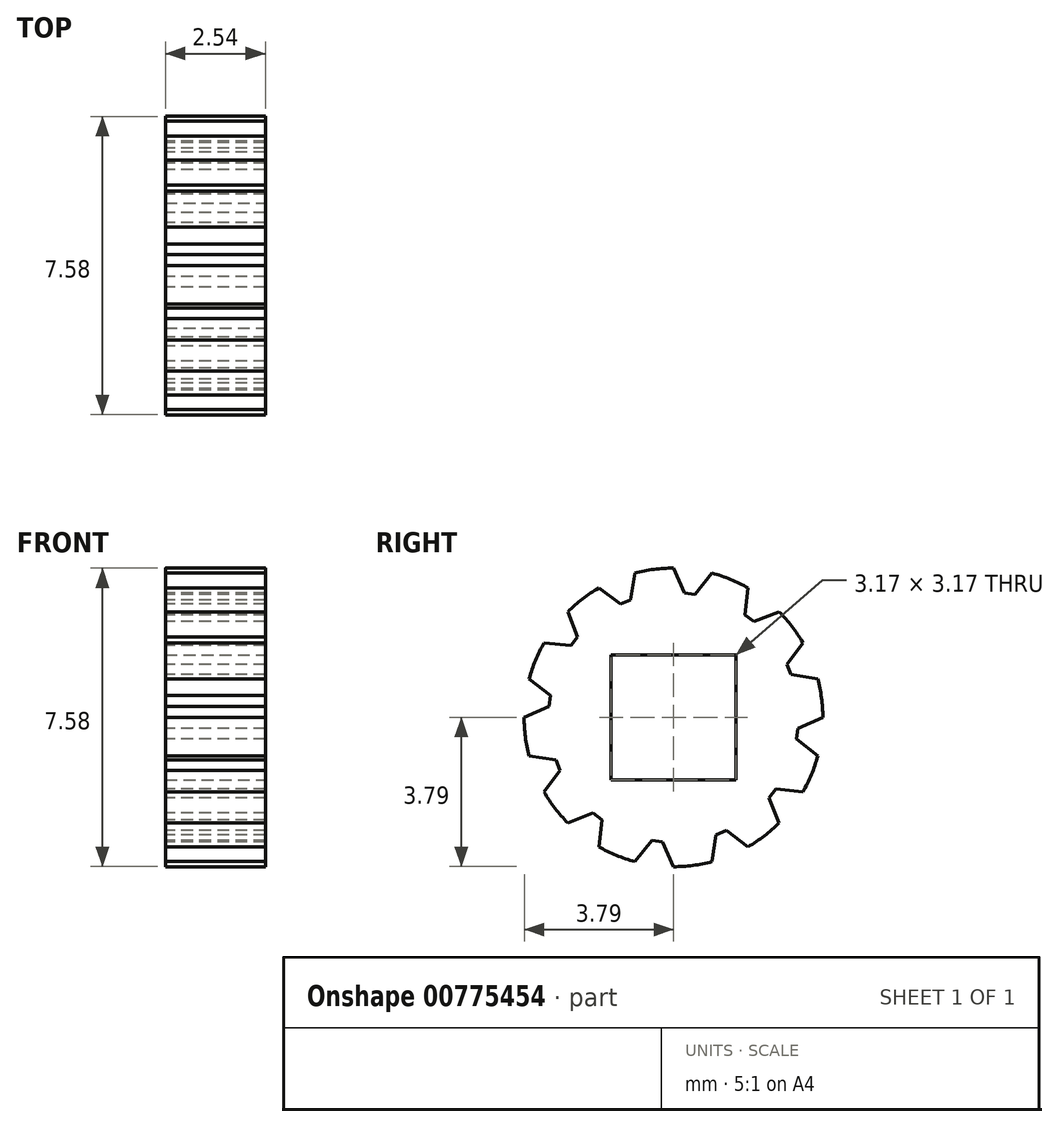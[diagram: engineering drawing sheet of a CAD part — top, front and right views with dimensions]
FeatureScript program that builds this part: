
annotation { "Feature Type Name" : "Feature", "Feature Type Description" : "" }
export const myFeature = defineFeature(function(context is Context, id is Id, definition is map)
    precondition{}
    {
        {
            var Q0;
            Q0=qCreatedBy(makeId("Right.planeOp"),FACE);
            var sketch = newSketch(context, id + "F0", { "sketchPlane" : qUnion([Q0])});
            skLineSegment(sketch, "E0", {"start": v(0, 0) * mm, "end": v(-3.8, 0) * mm});
            skLineSegment(sketch, "E1", {"start": v(0, 0) * mm, "end": v(-3.66, 0.98) * mm});
            skLineSegment(sketch, "E2", {"start": v(0, 0) * mm, "end": v(-3.16, 0.28) * mm});
            skLineSegment(sketch, "E3", {"start": v(0, 0) * mm, "end": v(-3.13, 0.55) * mm});
            skLineSegment(sketch, "E4", {"start": v(-3.16, 0.28) * mm, "end": v(-3.13, 0.55) * mm});
            skLineSegment(sketch, "E5", {"start": v(-3.13, 0.55) * mm, "end": v(-3.66, 0.98) * mm});
            skLineSegment(sketch, "E6", {"start": v(-3.16, 0.28) * mm, "end": v(-3.8, 0) * mm});
            skArc(sketch, "E7", {"start": v(-3.66, 0.98) * mm, "mid": v(-3.76, 0.5) * mm, "end": v(-3.8, 0) * mm});
            skArc(sketch, "E8", {"start": v(-3.8, 0) * mm, "mid": v(3.76, -0.5) * mm, "end": v(-3.66, 0.98) * mm});
            skArc(sketch, "E9.1.3", {"start": v(0.98, -3.66) * mm, "mid": v(1.45, -3.5) * mm, "end": v(1.9, -3.29) * mm});
            skArc(sketch, "E10.2.3", {"start": v(2.68, 2.68) * mm, "mid": v(2.3, 3) * mm, "end": v(1.9, 3.29) * mm});
            skArc(sketch, "E11.1.0", {"start": v(-3.66, -0.98) * mm, "mid": v(-3.5, -1.45) * mm, "end": v(-3.29, -1.9) * mm});
            skLineSegment(sketch, "E11.1.1", {"start": v(-2.98, -1.09) * mm, "end": v(-3.66, -0.98) * mm});
            skLineSegment(sketch, "E11.1.2", {"start": v(-2.88, -1.34) * mm, "end": v(-2.98, -1.09) * mm});
            skLineSegment(sketch, "E11.1.3", {"start": v(-2.88, -1.34) * mm, "end": v(-3.29, -1.9) * mm});
            skArc(sketch, "E11.2.0", {"start": v(-2.68, -2.68) * mm, "mid": v(-2.3, -3) * mm, "end": v(-1.9, -3.29) * mm});
            skLineSegment(sketch, "E11.2.1", {"start": v(-2.04, -2.43) * mm, "end": v(-2.68, -2.68) * mm});
            skLineSegment(sketch, "E11.2.2", {"start": v(-1.82, -2.6) * mm, "end": v(-2.04, -2.43) * mm});
            skLineSegment(sketch, "E11.2.3", {"start": v(-1.82, -2.6) * mm, "end": v(-1.9, -3.29) * mm});
            skArc(sketch, "E11.3.0", {"start": v(-0.98, -3.66) * mm, "mid": v(-0.5, -3.76) * mm, "end": v(0, -3.8) * mm});
            skLineSegment(sketch, "E11.3.1", {"start": v(-0.55, -3.13) * mm, "end": v(-0.98, -3.66) * mm});
            skLineSegment(sketch, "E11.3.2", {"start": v(-0.28, -3.16) * mm, "end": v(-0.55, -3.13) * mm});
            skLineSegment(sketch, "E11.3.3", {"start": v(-0.28, -3.16) * mm, "end": v(0, -3.8) * mm});
            skLineSegment(sketch, "E11.4.1", {"start": v(1.09, -2.98) * mm, "end": v(0.98, -3.66) * mm});
            skLineSegment(sketch, "E11.4.2", {"start": v(1.34, -2.88) * mm, "end": v(1.09, -2.98) * mm});
            skLineSegment(sketch, "E11.4.3", {"start": v(1.34, -2.88) * mm, "end": v(1.9, -3.29) * mm});
            skArc(sketch, "E11.5.0", {"start": v(2.68, -2.68) * mm, "mid": v(3, -2.3) * mm, "end": v(3.29, -1.9) * mm});
            skLineSegment(sketch, "E11.5.1", {"start": v(2.43, -2.04) * mm, "end": v(2.68, -2.68) * mm});
            skLineSegment(sketch, "E11.5.2", {"start": v(2.6, -1.82) * mm, "end": v(2.43, -2.04) * mm});
            skLineSegment(sketch, "E11.5.3", {"start": v(2.6, -1.82) * mm, "end": v(3.29, -1.9) * mm});
            skArc(sketch, "E11.6.0", {"start": v(3.66, -0.98) * mm, "mid": v(3.76, -0.5) * mm, "end": v(3.8, 0) * mm});
            skLineSegment(sketch, "E11.6.1", {"start": v(3.13, -0.55) * mm, "end": v(3.66, -0.98) * mm});
            skLineSegment(sketch, "E11.6.2", {"start": v(3.16, -0.28) * mm, "end": v(3.13, -0.55) * mm});
            skLineSegment(sketch, "E11.6.3", {"start": v(3.16, -0.28) * mm, "end": v(3.8, 0) * mm});
            skArc(sketch, "E11.7.0", {"start": v(3.66, 0.98) * mm, "mid": v(3.5, 1.45) * mm, "end": v(3.29, 1.9) * mm});
            skLineSegment(sketch, "E11.7.1", {"start": v(2.98, 1.09) * mm, "end": v(3.66, 0.98) * mm});
            skLineSegment(sketch, "E11.7.2", {"start": v(2.88, 1.34) * mm, "end": v(2.98, 1.09) * mm});
            skLineSegment(sketch, "E11.7.3", {"start": v(2.88, 1.34) * mm, "end": v(3.29, 1.9) * mm});
            skLineSegment(sketch, "E11.8.1", {"start": v(2.04, 2.43) * mm, "end": v(2.68, 2.68) * mm});
            skLineSegment(sketch, "E11.8.2", {"start": v(1.82, 2.6) * mm, "end": v(2.04, 2.43) * mm});
            skLineSegment(sketch, "E11.8.3", {"start": v(1.82, 2.6) * mm, "end": v(1.9, 3.29) * mm});
            skArc(sketch, "E11.9.0", {"start": v(0.98, 3.66) * mm, "mid": v(0.5, 3.76) * mm, "end": v(0, 3.8) * mm});
            skLineSegment(sketch, "E11.9.1", {"start": v(0.55, 3.13) * mm, "end": v(0.98, 3.66) * mm});
            skLineSegment(sketch, "E11.9.2", {"start": v(0.28, 3.16) * mm, "end": v(0.55, 3.13) * mm});
            skLineSegment(sketch, "E11.9.3", {"start": v(0.28, 3.16) * mm, "end": v(0, 3.8) * mm});
            skArc(sketch, "E11.10.0", {"start": v(-0.98, 3.66) * mm, "mid": v(-1.45, 3.5) * mm, "end": v(-1.9, 3.29) * mm});
            skLineSegment(sketch, "E11.10.1", {"start": v(-1.09, 2.98) * mm, "end": v(-0.98, 3.66) * mm});
            skLineSegment(sketch, "E11.10.2", {"start": v(-1.34, 2.88) * mm, "end": v(-1.09, 2.98) * mm});
            skLineSegment(sketch, "E11.10.3", {"start": v(-1.34, 2.88) * mm, "end": v(-1.9, 3.29) * mm});
            skArc(sketch, "E11.11.0", {"start": v(-2.68, 2.68) * mm, "mid": v(-3, 2.3) * mm, "end": v(-3.29, 1.9) * mm});
            skLineSegment(sketch, "E11.11.1", {"start": v(-2.43, 2.04) * mm, "end": v(-2.68, 2.68) * mm});
            skLineSegment(sketch, "E11.11.2", {"start": v(-2.6, 1.82) * mm, "end": v(-2.43, 2.04) * mm});
            skLineSegment(sketch, "E11.11.3", {"start": v(-2.6, 1.82) * mm, "end": v(-3.29, 1.9) * mm});
            skSolve(sketch);
        }
        {
            var Q0;
            {var subQ24=sQuery(id+"F0.wireOp",EDGE,"E0");Q0=makeQuery(id+"F0.imprint","IMPRINT",FACE,{"disambiguationData":[TD([[makeQuery(id+"F0.imprint","IMPRINT",EDGE,{"derivedFrom":subQ24}),1.0]])]});}
            var Q1;
            Q1=makeQuery(id+"F0.imprint","IMPRINT",FACE,{"disambiguationData":[TD([[makeQuery(id+"F0.imprint","IMPRINT",EDGE,{"derivedFrom":sQuery(id+"F0.wireOp",EDGE,"E0")}),-1.0]])]});
            var Q2;
            Q2=makeQuery(id+"F0.imprint","IMPRINT",FACE,{"disambiguationData":[TD([[makeQuery(id+"F0.imprint","IMPRINT",EDGE,{"derivedFrom":sQuery(id+"F0.wireOp",EDGE,"E2")}),-1.0]])]});
            var Q3;
            Q3=makeQuery(id+"F0.imprint","IMPRINT",FACE,{"disambiguationData":[TD([[makeQuery(id+"F0.imprint","IMPRINT",EDGE,{"derivedFrom":sQuery(id+"F0.wireOp",EDGE,"E1")}),1.0]])]});
            extrude(context, id + "F1", {"entities" : qUnion([Q0, Q1, Q2, Q3]), "depth" : 2.54 * mm, "offsetDistance" : 25.4 * mm});
        }
        {
            var Q0;
            Q0=makeQuery(id+"F1.opExtrude","CAP_FACE",FACE,{"disambiguationData":[OSD([sQuery(id+"F0.wireOp",EDGE,"E4"),sQuery(id+"F0.wireOp",EDGE,"E5"),sQuery(id+"F0.wireOp",EDGE,"E6"),sQuery(id+"F0.wireOp",EDGE,"E8"),sQuery(id+"F0.wireOp",EDGE,"E11.1.1"),sQuery(id+"F0.wireOp",EDGE,"E11.1.2"),sQuery(id+"F0.wireOp",EDGE,"E11.1.3"),sQuery(id+"F0.wireOp",EDGE,"E11.2.1"),sQuery(id+"F0.wireOp",EDGE,"E11.2.2"),sQuery(id+"F0.wireOp",EDGE,"E11.2.3"),sQuery(id+"F0.wireOp",EDGE,"E11.3.1"),sQuery(id+"F0.wireOp",EDGE,"E11.3.2"),sQuery(id+"F0.wireOp",EDGE,"E11.3.3"),sQuery(id+"F0.wireOp",EDGE,"E11.4.1"),sQuery(id+"F0.wireOp",EDGE,"E11.4.2"),sQuery(id+"F0.wireOp",EDGE,"E11.4.3"),sQuery(id+"F0.wireOp",EDGE,"E11.5.1"),sQuery(id+"F0.wireOp",EDGE,"E11.5.2"),sQuery(id+"F0.wireOp",EDGE,"E11.5.3"),sQuery(id+"F0.wireOp",EDGE,"E11.6.1"),sQuery(id+"F0.wireOp",EDGE,"E11.6.2"),sQuery(id+"F0.wireOp",EDGE,"E11.6.3"),sQuery(id+"F0.wireOp",EDGE,"E11.7.1"),sQuery(id+"F0.wireOp",EDGE,"E11.7.2"),sQuery(id+"F0.wireOp",EDGE,"E11.7.3"),sQuery(id+"F0.wireOp",EDGE,"E11.8.1"),sQuery(id+"F0.wireOp",EDGE,"E11.8.2"),sQuery(id+"F0.wireOp",EDGE,"E11.8.3"),sQuery(id+"F0.wireOp",EDGE,"E11.9.1"),sQuery(id+"F0.wireOp",EDGE,"E11.9.2"),sQuery(id+"F0.wireOp",EDGE,"E11.9.3"),sQuery(id+"F0.wireOp",EDGE,"E11.10.1"),sQuery(id+"F0.wireOp",EDGE,"E11.10.2"),sQuery(id+"F0.wireOp",EDGE,"E11.10.3"),sQuery(id+"F0.wireOp",EDGE,"E11.11.1"),sQuery(id+"F0.wireOp",EDGE,"E11.11.2"),sQuery(id+"F0.wireOp",EDGE,"E11.11.3")])],"isStart":false});
            var sketch = newSketch(context, id + "F2", { "sketchPlane" : qUnion([Q0])});
            skLineSegment(sketch, "E12.bottom", {"start": v(-1.59, 1.59) * mm, "end": v(1.59, 1.59) * mm});
            skLineSegment(sketch, "E12.top", {"start": v(-1.59, -1.59) * mm, "end": v(1.59, -1.59) * mm});
            skLineSegment(sketch, "E12.left", {"start": v(-1.59, 1.59) * mm, "end": v(-1.59, -1.59) * mm});
            skLineSegment(sketch, "E12.right", {"start": v(1.59, 1.59) * mm, "end": v(1.59, -1.59) * mm});
            skPoint(sketch, "E12.middle", {"position": v(0, 0) * mm});
            skSolve(sketch);
        }
        {
            var Q0;
            Q0=makeQuery(id+"F2.imprint","IMPRINT",FACE,{"disambiguationData":[TD([[makeQuery(id+"F2.imprint","IMPRINT",EDGE,{"derivedFrom":sQuery(id+"F2.wireOp",EDGE,"E12.bottom")}),-1.0]])]});
            extrude(context, id + "F3", {"entities" : qUnion([Q0]), "operationType" : NewBodyOperationType.REMOVE, "oppositeDirection" : true, "depth" : 25.4 * mm, "offsetDistance" : 25.4 * mm});
        }
    });
